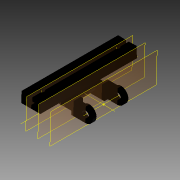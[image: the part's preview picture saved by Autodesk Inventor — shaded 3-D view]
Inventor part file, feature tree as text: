
AUTODESK INVENTOR PART (.ipt)
format: ipt  version: 2015 (Build 190159000, 159)  size: 176,128 bytes
history: native  units: in
note: dims shown in document units (in); Inventor stores cm internally (conversion verified against a paired STEP export)
features: other x18, plane x3, imported_body x1
ambient origin geometry x8: Origin, YZ Plane, XZ Plane, XY Plane, X Axis, Y Axis, Z Axis, Center Point
bodies: Body1 (feature_tree)
feature tree (22):
  other  "tetrix_736468_tt_link_2012"
  other  "tetrix_736468_tt_link_20121"
  other  "PNT0"
  other  "PNT1"
  other  "A_1"
  other  "A_2"
  other  "A_3"
  other  "A_4"
  other  "A_5"
  other  "A_6"
  other  "FRONT"
  other  "TOP"
  other  "RIGHT"
  other  "DTM1"
  other  "DTM2"
  other  "Work Axis7"
  other  "Work Axis8"
  plane  "Work Plane6"
  other  "Work Point3"
  plane  "Work Plane7"
  plane  "Work Plane8"
  imported_body  "Base1"
